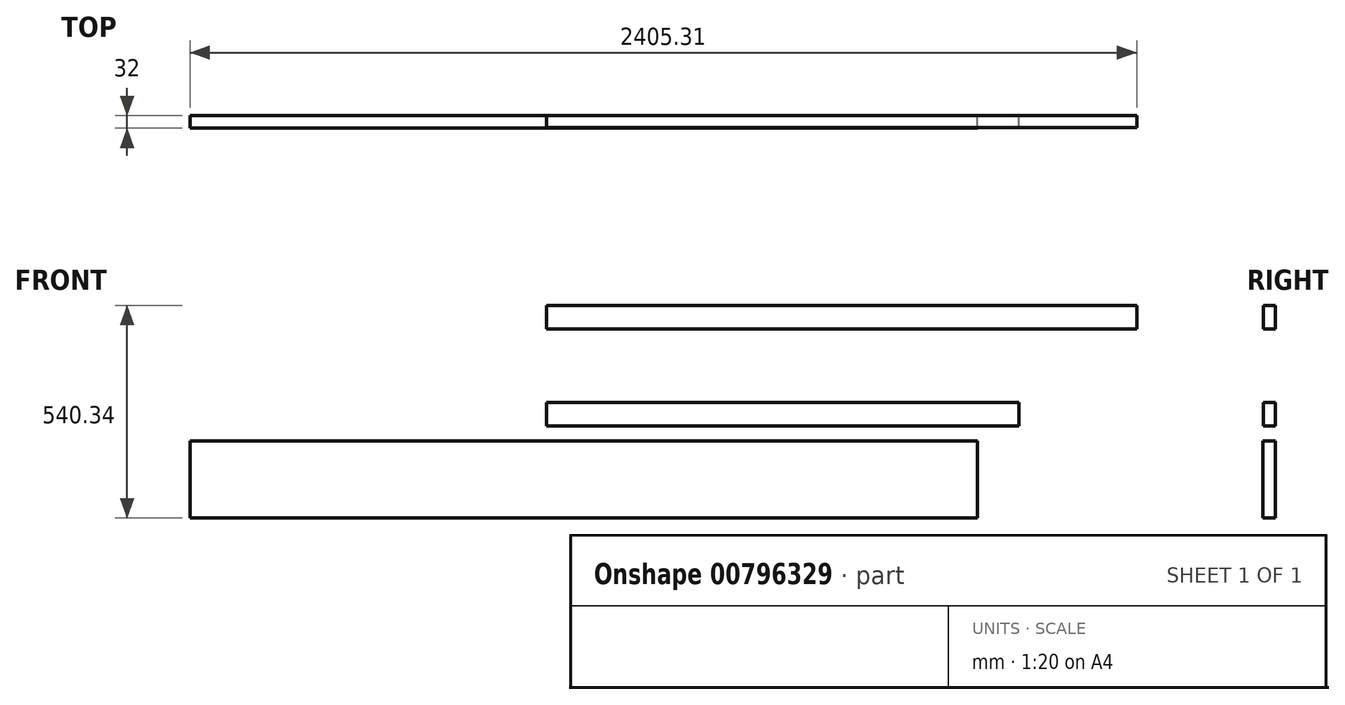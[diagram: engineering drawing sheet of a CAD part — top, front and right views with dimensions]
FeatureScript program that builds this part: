
annotation { "Feature Type Name" : "Feature", "Feature Type Description" : "" }
export const myFeature = defineFeature(function(context is Context, id is Id, definition is map)
    precondition{}
    {
        {
            var Q0;
            Q0=qCreatedBy(makeId("Front.planeOp"),FACE);
            var sketch = newSketch(context, id + "F0", { "sketchPlane" : qUnion([Q0])});
            skLineSegment(sketch, "E0.bottom", {"start": v(0, 3.38) * mm, "end": v(1500, 3.38) * mm});
            skLineSegment(sketch, "E0.top", {"start": v(0, 63.38) * mm, "end": v(1500, 63.38) * mm});
            skLineSegment(sketch, "E0.left", {"start": v(0, 3.38) * mm, "end": v(0, 63.38) * mm});
            skLineSegment(sketch, "E0.right", {"start": v(1500, 3.38) * mm, "end": v(1500, 63.38) * mm});
            skLineSegment(sketch, "E1.bottom", {"start": v(0, 63.38) * mm, "end": v(300, 63.38) * mm});
            skLineSegment(sketch, "E1.top", {"start": v(0, 3.38) * mm, "end": v(300, 3.38) * mm});
            skLineSegment(sketch, "E1.left", {"start": v(0, 63.38) * mm, "end": v(0, 3.38) * mm});
            skLineSegment(sketch, "E1.right", {"start": v(300, 63.38) * mm, "end": v(300, 3.38) * mm});
            skSolve(sketch);
        }
        {
            var Q0;
            Q0 = qSketchRegion(id + "F0", true);
            extrude(context, id + "F1", {"entities" : qUnion([Q0]), "depth" : 30 * mm, "offsetDistance" : 25 * mm});
        }
        {
            var Q0;
            Q0=qCreatedBy(makeId("Front.planeOp"),FACE);
            var sketch = newSketch(context, id + "F2", { "sketchPlane" : qUnion([Q0])});
            skLineSegment(sketch, "E2.bottom", {"start": v(0, -183.4) * mm, "end": v(1200, -183.4) * mm});
            skLineSegment(sketch, "E2.top", {"start": v(0, -243.4) * mm, "end": v(1200, -243.4) * mm});
            skLineSegment(sketch, "E2.left", {"start": v(0, -183.4) * mm, "end": v(0, -243.4) * mm});
            skLineSegment(sketch, "E2.right", {"start": v(1200, -183.4) * mm, "end": v(1200, -243.4) * mm});
            skSolve(sketch);
        }
        {
            var Q0;
            Q0 = qSketchRegion(id + "F2", true);
            extrude(context, id + "F3", {"entities" : qUnion([Q0]), "depth" : 30 * mm, "offsetDistance" : 25 * mm});
        }
        {
            var Q0;
            Q0=qCreatedBy(makeId("Front.planeOp"),FACE);
            var sketch = newSketch(context, id + "F4", { "sketchPlane" : qUnion([Q0])});
            skLineSegment(sketch, "E3.bottom", {"start": v(-905.31, -281.96) * mm, "end": v(1094.69, -281.96) * mm});
            skLineSegment(sketch, "E3.top", {"start": v(-905.31, -476.96) * mm, "end": v(1094.69, -476.96) * mm});
            skLineSegment(sketch, "E3.left", {"start": v(-905.31, -281.96) * mm, "end": v(-905.31, -476.96) * mm});
            skLineSegment(sketch, "E3.right", {"start": v(1094.69, -281.96) * mm, "end": v(1094.69, -476.96) * mm});
            skSolve(sketch);
        }
        {
            var Q0;
            Q0 = qSketchRegion(id + "F4", true);
            extrude(context, id + "F5", {"entities" : qUnion([Q0]), "depth" : 32 * mm, "offsetDistance" : 25 * mm});
        }
    });
